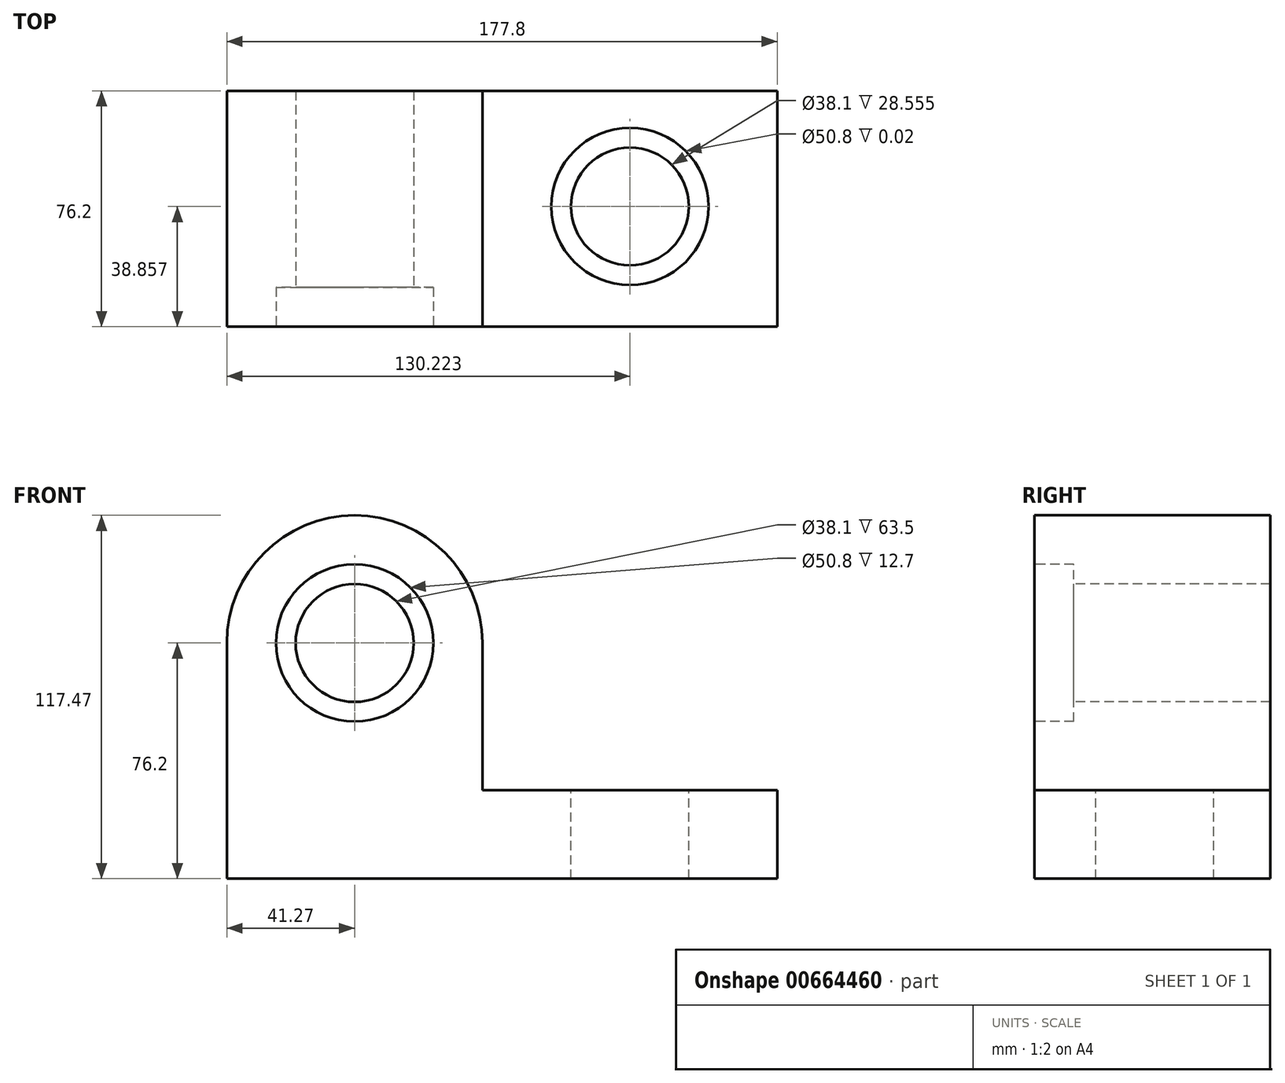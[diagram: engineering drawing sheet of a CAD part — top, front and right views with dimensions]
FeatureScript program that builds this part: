
annotation { "Feature Type Name" : "Feature", "Feature Type Description" : "" }
export const myFeature = defineFeature(function(context is Context, id is Id, definition is map)
    precondition{}
    {
        {
            var Q0;
            Q0=qCreatedBy(makeId("Front.planeOp"),FACE);
            var sketch = newSketch(context, id + "F0", { "sketchPlane" : qUnion([Q0])});
            skCircle(sketch, "E0", {"center": v(0, 0) * mm, "radius": 19.05 * mm});
            skCircle(sketch, "E1", {"center": v(0, 0) * mm, "radius": 41.28 * mm});
            skLineSegment(sketch, "E2", {"start": v(-41.28, 0) * mm, "end": v(-41.27, -76.2) * mm});
            skLineSegment(sketch, "E3", {"start": v(41.27, 0) * mm, "end": v(41.28, -76.2) * mm});
            skLineSegment(sketch, "E4", {"start": v(-41.28, -76.2) * mm, "end": v(136.53, -76.2) * mm});
            skLineSegment(sketch, "E5", {"start": v(136.53, -76.2) * mm, "end": v(136.53, -47.62) * mm});
            skLineSegment(sketch, "E6", {"start": v(136.53, -47.62) * mm, "end": v(41.28, -47.62) * mm});
            skSolve(sketch);
        }
        {
            var Q0;
            Q0=makeQuery(id+"F0.imprint","IMPRINT",FACE,{"disambiguationData":[TD([[makeQuery(id+"F0.imprint","IMPRINT",EDGE,{"derivedFrom":sQuery(id+"F0.wireOp",EDGE,"E0")}),-1.0]])]});
            var Q1;
            {var subQ6=sQuery(id+"F0.wireOp",EDGE,"E2");Q1=makeQuery(id+"F0.imprint","IMPRINT",FACE,{"disambiguationData":[TD([[makeQuery(id+"F0.imprint","IMPRINT",EDGE,{"derivedFrom":subQ6}),1.0]])]});}
            var Q2;
            {var subQ4=sQuery(id+"F0.wireOp",EDGE,"E5");Q2=makeQuery(id+"F0.imprint","IMPRINT",FACE,{"disambiguationData":[TD([[makeQuery(id+"F0.imprint","IMPRINT",EDGE,{"derivedFrom":subQ4}),1.0]])]});}
            var Q3;
            Q3=makeQuery(id+"F0.imprint","IMPRINT",FACE,{"disambiguationData":[TD([[makeQuery(id+"F0.imprint","IMPRINT",EDGE,{"derivedFrom":sQuery(id+"F0.wireOp",EDGE,"E0")}),1.0]])]});
            extrude(context, id + "F1", {"entities" : qUnion([Q0, Q1, Q2, Q3]), "oppositeDirection" : true, "depth" : 76.2 * mm});
        }
        {
            var Q0;
            Q0=makeQuery(id+"F1.opExtrude","SWEPT_FACE",FACE,{"disambiguationData":[OSD([sQuery(id+"F0.wireOp",EDGE,"E6")])]});
            var sketch = newSketch(context, id + "F2", { "sketchPlane" : qUnion([Q0])});
            skCircle(sketch, "E7", {"center": v(88.95, 38.86) * mm, "radius": 19.05 * mm});
            skSolve(sketch);
        }
        {
            var Q0;
            Q0=sQuery(id+"F2.wireOp",VERTEX,"E7.center");
            var Q1;
            Q1=makeQuery(id+"F1.opExtrude","SWEPT_BODY",BODY,{"disambiguationData":[OSD([sQuery(id+"F0.wireOp",EDGE,"E1"),sQuery(id+"F0.wireOp",EDGE,"E2"),sQuery(id+"F0.wireOp",EDGE,"E3"),sQuery(id+"F0.wireOp",EDGE,"E4"),sQuery(id+"F0.wireOp",EDGE,"E5"),sQuery(id+"F0.wireOp",EDGE,"E6")])]});
            hole(context, id + "F3", {"style" : HoleStyle.C_BORE, "endStyle" : HoleEndStyle.THROUGH, "holeDiameter" : 38.1 * mm, "cBoreDiameter" : 50.8 * mm, "cBoreDepth" : 1 / 50.8 * mm, "isTappedThrough" : true, "tappedDepth" : 12.7 * mm, "tapClearance" : 3, "locations" : qUnion([Q0]), "scope" : qUnion([Q1])});
        }
        {
            var Q0;
            Q0=qSketchRegion(id+"F0",true);
            var sketch = newSketch(context, id + "F4", { "sketchPlane" : qUnion([Q0])});
            skCircle(sketch, "E8", {"center": v(0, 0) * mm, "radius": 7.1 * mm});
            skSolve(sketch);
        }
        {
            var Q0;
            Q0=sQuery(id+"F4.wireOp",VERTEX,"E8.center");
            var Q1;
            Q1=makeQuery(id+"F1.opExtrude","SWEPT_BODY",BODY,{"disambiguationData":[OSD([sQuery(id+"F0.wireOp",EDGE,"E1"),sQuery(id+"F0.wireOp",EDGE,"E2"),sQuery(id+"F0.wireOp",EDGE,"E3"),sQuery(id+"F0.wireOp",EDGE,"E4"),sQuery(id+"F0.wireOp",EDGE,"E5"),sQuery(id+"F0.wireOp",EDGE,"E6")])]});
            hole(context, id + "F5", {"style" : HoleStyle.C_BORE, "endStyle" : HoleEndStyle.THROUGH, "holeDiameter" : 38.1 * mm, "cBoreDiameter" : 50.8 * mm, "cBoreDepth" : 12.7 * mm, "isTappedThrough" : true, "tappedDepth" : 12.7 * mm, "tapClearance" : 3, "locations" : qUnion([Q0]), "scope" : qUnion([Q1])});
        }
    });
